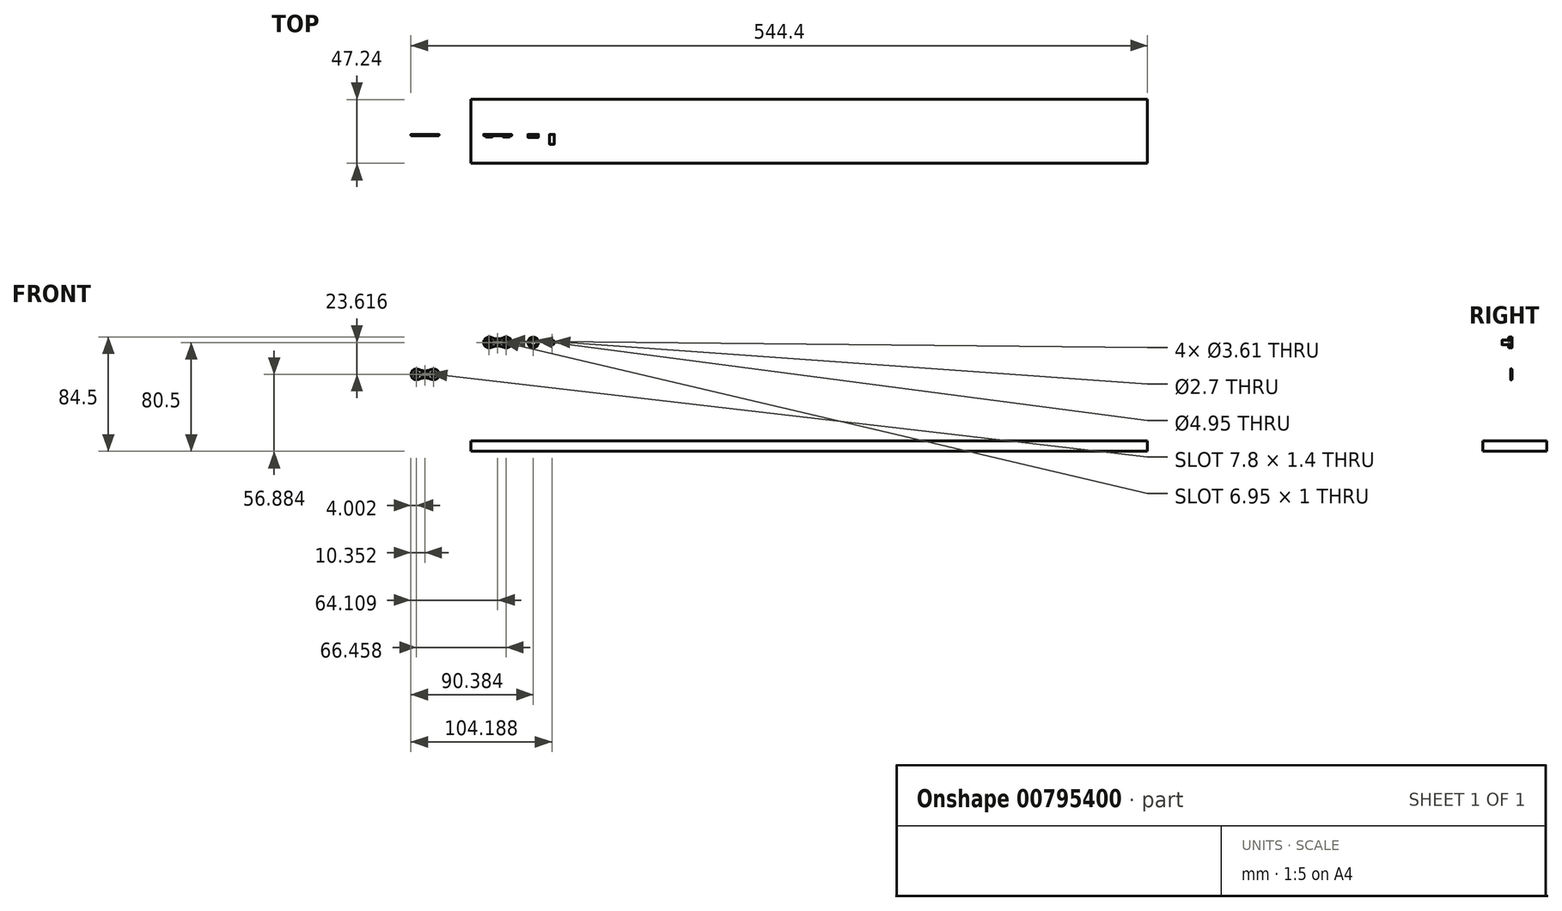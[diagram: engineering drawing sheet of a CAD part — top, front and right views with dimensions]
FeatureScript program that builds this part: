
annotation { "Feature Type Name" : "Feature", "Feature Type Description" : "" }
export const myFeature = defineFeature(function(context is Context, id is Id, definition is map)
    precondition{}
    {
        {
            var Q0;
            Q0=qCreatedBy(makeId("Front.planeOp"),FACE);
            var sketch = newSketch(context, id + "F0", { "sketchPlane" : qUnion([Q0])});
            skCircle(sketch, "E0", {"center": v(-38.42, 0) * mm, "radius": 3.85 * mm});
            skCircle(sketch, "E1", {"center": v(-38.42, 0) * mm, "radius": 2.75 * mm});
            skPoint(sketch, "E2", {"position": v(13.36, 0) * mm});
            skCircle(sketch, "E3", {"center": v(13.36, 0) * mm, "radius": 1.8 * mm});
            skCircle(sketch, "E4", {"center": v(26.06, 0) * mm, "radius": 1.8 * mm});
            skCircle(sketch, "E5", {"center": v(26.06, 0) * mm, "radius": 2.48 * mm});
            skCircle(sketch, "E6", {"center": v(13.36, 0) * mm, "radius": 2.48 * mm});
            skArc(sketch, "E7", {"start": v(24.35, -3.61) * mm, "mid": v(30.06, 0) * mm, "end": v(24.35, 3.61) * mm});
            skArc(sketch, "E8", {"start": v(15.07, 3.61) * mm, "mid": v(9.36, 0) * mm, "end": v(15.07, -3.61) * mm});
            skLineSegment(sketch, "E9", {"start": v(19.7, 13.4) * mm, "end": v(19.7, 17.02) * mm});
            skArc(sketch, "E10", {"start": v(15.07, 3.61) * mm, "mid": v(19.7, 2.57) * mm, "end": v(24.35, 3.61) * mm});
            skArc(sketch, "E11.MirrorCS", {"start": v(15.07, -3.61) * mm, "mid": v(19.7, -2.57) * mm, "end": v(24.35, -3.61) * mm});
            skCircle(sketch, "E12", {"center": v(45.98, 0) * mm, "radius": 2.48 * mm});
            skCircle(sketch, "E13", {"center": v(45.98, 0) * mm, "radius": 3.9 * mm});
            skCircle(sketch, "E14", {"center": v(59.79, 0) * mm, "radius": 1.8 * mm});
            skCircle(sketch, "E15", {"center": v(59.79, 0) * mm, "radius": 1.35 * mm});
            skLineSegment(sketch, "E16", {"start": v(23.58, 0) * mm, "end": v(15.83, 0) * mm});
            skPoint(sketch, "E17", {"position": v(22.68, 0) * mm});
            skPoint(sketch, "E18.MirrorP", {"position": v(16.74, 0) * mm});
            skLineSegment(sketch, "E19", {"start": v(22.68, 0) * mm, "end": v(16.74, 0) * mm});
            skArc(sketch, "E20.0.startCap", {"start": v(22.68, 0.5) * mm, "mid": v(23.18, 0) * mm, "end": v(22.68, -0.5) * mm});
            skArc(sketch, "E20.0.endCap", {"start": v(16.74, -0.5) * mm, "mid": v(16.24, 0) * mm, "end": v(16.74, 0.5) * mm});
            skLineSegment(sketch, "E20.0.left", {"start": v(22.68, -0.5) * mm, "end": v(16.74, -0.5) * mm});
            skLineSegment(sketch, "E20.0.right", {"start": v(22.68, 0.5) * mm, "end": v(16.74, 0.5) * mm});
            skSolve(sketch);
        }
        {
            var Q0;
            Q0=makeQuery(id+"F0.imprint","IMPRINT",FACE,{"disambiguationData":[TD([[makeQuery(id+"F0.imprint","IMPRINT",EDGE,{"derivedFrom":sQuery(id+"F0.wireOp",EDGE,"E5")}),-1.0]])]});
            extrude(context, id + "F1", {"entities" : qUnion([Q0]), "depth" : .95 * mm, "offsetDistance" : 25 * mm});
        }
        {
            var Q0;
            Q0=makeQuery(id+"F0.imprint","IMPRINT",FACE,{"disambiguationData":[TD([[makeQuery(id+"F0.imprint","IMPRINT",EDGE,{"derivedFrom":sQuery(id+"F0.wireOp",EDGE,"E3")}),-1.0]])]});
            var Q1;
            Q1=makeQuery(id+"F0.imprint","IMPRINT",FACE,{"disambiguationData":[TD([[makeQuery(id+"F0.imprint","IMPRINT",EDGE,{"derivedFrom":sQuery(id+"F0.wireOp",EDGE,"E4")}),-1.0]])]});
            extrude(context, id + "F2", {"entities" : qUnion([Q0, Q1]), "operationType" : NewBodyOperationType.ADD, "depth" : 2 * mm, "offsetDistance" : 25 * mm});
        }
        {
            var Q0;
            Q0=makeQuery(id+"F2.opExtrude","CAP_EDGE",EDGE,{"disambiguationData":[OSD([sQuery(id+"F0.wireOp",EDGE,"E3")])],"isStart":true});
            var Q1;
            Q1=makeQuery(id+"F2.opExtrude","CAP_EDGE",EDGE,{"disambiguationData":[OSD([sQuery(id+"F0.wireOp",EDGE,"E4")])],"isStart":true});
            fillet(context, id + "F3", {"entities" : qUnion([Q0, Q1]), "radius" : .5 * mm, "tangentPropagation" : true, "allowEdgeOverflow" : false});
        }
        {
            var Q0;
            Q0=makeQuery(id+"F0.imprint","IMPRINT",FACE,{"disambiguationData":[TD([[makeQuery(id+"F0.imprint","IMPRINT",EDGE,{"derivedFrom":sQuery(id+"F0.wireOp",EDGE,"E12")}),-1.0]])]});
            extrude(context, id + "F4", {"entities" : qUnion([Q0]), "depth" : 2.3 * mm, "offsetDistance" : 25 * mm});
        }
        {
            var Q0;
            Q0=makeQuery(id+"F0.imprint","IMPRINT",FACE,{"disambiguationData":[TD([[makeQuery(id+"F0.imprint","IMPRINT",EDGE,{"derivedFrom":sQuery(id+"F0.wireOp",EDGE,"E14")}),1.0]])]});
            extrude(context, id + "F5", {"entities" : qUnion([Q0]), "depth" : 7.28 * mm, "offsetDistance" : 25 * mm});
        }
        {
            var Q0;
            Q0=makeQuery(id+"F4.opExtrude","CAP_FACE",FACE,{"disambiguationData":[OSD([sQuery(id+"F0.wireOp",EDGE,"E12"),sQuery(id+"F0.wireOp",EDGE,"E13")])],"isStart":false});
            var Q1;
            Q1=makeQuery(id+"F4.opExtrude","CAP_FACE",FACE,{"disambiguationData":[OSD([sQuery(id+"F0.wireOp",EDGE,"E12"),sQuery(id+"F0.wireOp",EDGE,"E13")])],"isStart":true});
            var Q2;
            Q2=makeQuery(id+"F5.opExtrude","CAP_FACE",FACE,{"disambiguationData":[OSD([sQuery(id+"F0.wireOp",EDGE,"E14")])],"isStart":false});
            var Q3;
            Q3=makeQuery(id+"F5.opExtrude","CAP_FACE",FACE,{"disambiguationData":[OSD([sQuery(id+"F0.wireOp",EDGE,"E14")])],"isStart":true});
            fillet(context, id + "F6", {"entities" : qUnion([Q0, Q1, Q2, Q3]), "radius" : .2 * mm, "tangentPropagation" : true, "allowEdgeOverflow" : false});
        }
        {
            var Q0;
            Q0=qCreatedBy(makeId("Front.planeOp"),FACE);
            var sketch = newSketch(context, id + "F7", { "sketchPlane" : qUnion([Q0])});
            skPoint(sketch, "E21", {"position": v(-40.4, -23.62) * mm});
            skCircle(sketch, "E22", {"center": v(-40.4, -23.62) * mm, "radius": 1.8 * mm});
            skCircle(sketch, "E23", {"center": v(-27.7, -23.62) * mm, "radius": 1.8 * mm});
            skArc(sketch, "E24", {"start": v(-29.41, -27.23) * mm, "mid": v(-23.7, -23.62) * mm, "end": v(-29.41, -20) * mm});
            skArc(sketch, "E25", {"start": v(-38.68, -20) * mm, "mid": v(-44.4, -23.62) * mm, "end": v(-38.68, -27.23) * mm});
            skArc(sketch, "E26", {"start": v(-38.68, -20) * mm, "mid": v(-34.05, -21.05) * mm, "end": v(-29.41, -20) * mm});
            skArc(sketch, "E27.MirrorCS", {"start": v(-38.68, -27.23) * mm, "mid": v(-34.05, -26.19) * mm, "end": v(-29.41, -27.23) * mm});
            skPoint(sketch, "E28.start.orphan", {"position": v(-34.05, -21.05) * mm});
            skLineSegment(sketch, "E29", {"start": v(-30.85, -23.62) * mm, "end": v(-37.25, -23.62) * mm});
            skPoint(sketch, "E30", {"position": v(-30.85, -23.62) * mm});
            skPoint(sketch, "E31.MirrorP", {"position": v(-37.25, -23.62) * mm});
            skArc(sketch, "E32.0.startCap", {"start": v(-30.85, -23.12) * mm, "mid": v(-30.35, -23.62) * mm, "end": v(-30.85, -24.12) * mm});
            skArc(sketch, "E32.0.endCap", {"start": v(-37.25, -24.12) * mm, "mid": v(-37.75, -23.62) * mm, "end": v(-37.25, -23.12) * mm});
            skLineSegment(sketch, "E32.0.left", {"start": v(-30.85, -24.12) * mm, "end": v(-37.25, -24.12) * mm});
            skLineSegment(sketch, "E32.0.right", {"start": v(-30.85, -23.12) * mm, "end": v(-37.25, -23.12) * mm});
            skSolve(sketch);
        }
        {
            var Q0;
            Q0 = qSketchRegion(id + "F7", true);
            extrude(context, id + "F8", {"entities" : qUnion([Q0]), "depth" : .95 * mm, "offsetDistance" : 25 * mm});
        }
        {
            var Q0;
            Q0=makeQuery(id+"F8.opExtrude","CAP_FACE",FACE,{"disambiguationData":[OSD([sQuery(id+"F7.wireOp",EDGE,"3b588936-2929-49d6-83d5-eb2522ade748"),sQuery(id+"F7.wireOp",EDGE,"00c4337e-04a4-4787-859e-60a6f2e1b418"),sQuery(id+"F7.wireOp",EDGE,"E24"),sQuery(id+"F7.wireOp",EDGE,"E25"),sQuery(id+"F7.wireOp",EDGE,"E26"),sQuery(id+"F7.wireOp",EDGE,"E27.MirrorCS")])],"isStart":false});
            var Q1;
            Q1=makeQuery(id+"F8.opExtrude","CAP_FACE",FACE,{"disambiguationData":[OSD([sQuery(id+"F7.wireOp",EDGE,"3b588936-2929-49d6-83d5-eb2522ade748"),sQuery(id+"F7.wireOp",EDGE,"00c4337e-04a4-4787-859e-60a6f2e1b418"),sQuery(id+"F7.wireOp",EDGE,"E24"),sQuery(id+"F7.wireOp",EDGE,"E25"),sQuery(id+"F7.wireOp",EDGE,"E26"),sQuery(id+"F7.wireOp",EDGE,"E27.MirrorCS")])],"isStart":true});
            fillet(context, id + "F9", {"entities" : qUnion([Q0, Q1]), "radius" : .2 * mm, "tangentPropagation" : true, "allowEdgeOverflow" : false});
        }
        {
            var Q0;
            Q0=makeQuery(id+"F1.opExtrude","CAP_EDGE",EDGE,{"disambiguationData":[OSD([sQuery(id+"F0.wireOp",EDGE,"E8")])],"isStart":true});
            var Q1;
            Q1=makeQuery(id+"F2.opExtrude","CAP_EDGE",EDGE,{"disambiguationData":[OSD([sQuery(id+"F0.wireOp",EDGE,"E6")])],"isStart":false});
            var Q2;
            Q2=makeQuery(id+"F2.opExtrude","CAP_EDGE",EDGE,{"disambiguationData":[OSD([sQuery(id+"F0.wireOp",EDGE,"E3")])],"isStart":false});
            var Q3;
            Q3=makeQuery(id+"F1.opExtrude","CAP_EDGE",EDGE,{"disambiguationData":[OSD([sQuery(id+"F0.wireOp",EDGE,"E11.MirrorCS")])],"isStart":false});
            var Q4;
            Q4=makeQuery(id+"F1.opExtrude","CAP_EDGE",EDGE,{"disambiguationData":[OSD([sQuery(id+"F0.wireOp",EDGE,"E8")])],"isStart":false});
            var Q5;
            Q5=makeQuery(id+"F1.opExtrude","CAP_EDGE",EDGE,{"disambiguationData":[OSD([sQuery(id+"F0.wireOp",EDGE,"E7")])],"isStart":false});
            var Q6;
            Q6=makeQuery(id+"F2.opExtrude","CAP_EDGE",EDGE,{"disambiguationData":[OSD([sQuery(id+"F0.wireOp",EDGE,"E4")])],"isStart":false});
            var Q7;
            Q7=makeQuery(id+"F2.opExtrude","CAP_EDGE",EDGE,{"disambiguationData":[OSD([sQuery(id+"F0.wireOp",EDGE,"E5")])],"isStart":false});
            var Q8;
            Q8=makeQuery(id+"F1.opExtrude","CAP_EDGE",EDGE,{"disambiguationData":[OSD([sQuery(id+"F0.wireOp",EDGE,"E10")])],"isStart":false});
            var Q9;
            Q9=makeQuery(id+"F1.opExtrude","CAP_EDGE",EDGE,{"disambiguationData":[OSD([sQuery(id+"F0.wireOp",EDGE,"E10")])],"isStart":true});
            var Q10;
            Q10=makeQuery(id+"F1.opExtrude","CAP_EDGE",EDGE,{"disambiguationData":[OSD([sQuery(id+"F0.wireOp",EDGE,"E7")])],"isStart":true});
            var Q11;
            Q11=makeQuery(id+"F1.opExtrude","CAP_EDGE",EDGE,{"disambiguationData":[OSD([sQuery(id+"F0.wireOp",EDGE,"E11.MirrorCS")])],"isStart":true});
            fillet(context, id + "F10", {"entities" : qUnion([Q0, Q1, Q2, Q3, Q4, Q5, Q6, Q7, Q8, Q9, Q10, Q11]), "radius" : .2 * mm, "tangentPropagation" : true, "allowEdgeOverflow" : false});
        }
        {
            var Q0;
            Q0=qCreatedBy(makeId("Right.planeOp"),FACE);
            var sketch = newSketch(context, id + "F11", { "sketchPlane" : qUnion([Q0])});
            skLineSegment(sketch, "E33.bottom", {"start": v(-21.49, -72.78) * mm, "end": v(25.75, -72.78) * mm});
            skLineSegment(sketch, "E33.top", {"start": v(-21.49, -80.5) * mm, "end": v(25.75, -80.5) * mm});
            skLineSegment(sketch, "E33.left", {"start": v(-21.49, -72.78) * mm, "end": v(-21.49, -80.5) * mm});
            skLineSegment(sketch, "E33.right", {"start": v(25.75, -72.78) * mm, "end": v(25.75, -80.5) * mm});
            skSolve(sketch);
        }
        {
            var Q0;
            Q0 = qSketchRegion(id + "F11", true);
            extrude(context, id + "F12", {"entities" : qUnion([Q0]), "depth" : 500 * mm, "offsetDistance" : 25 * mm});
        }
    });
